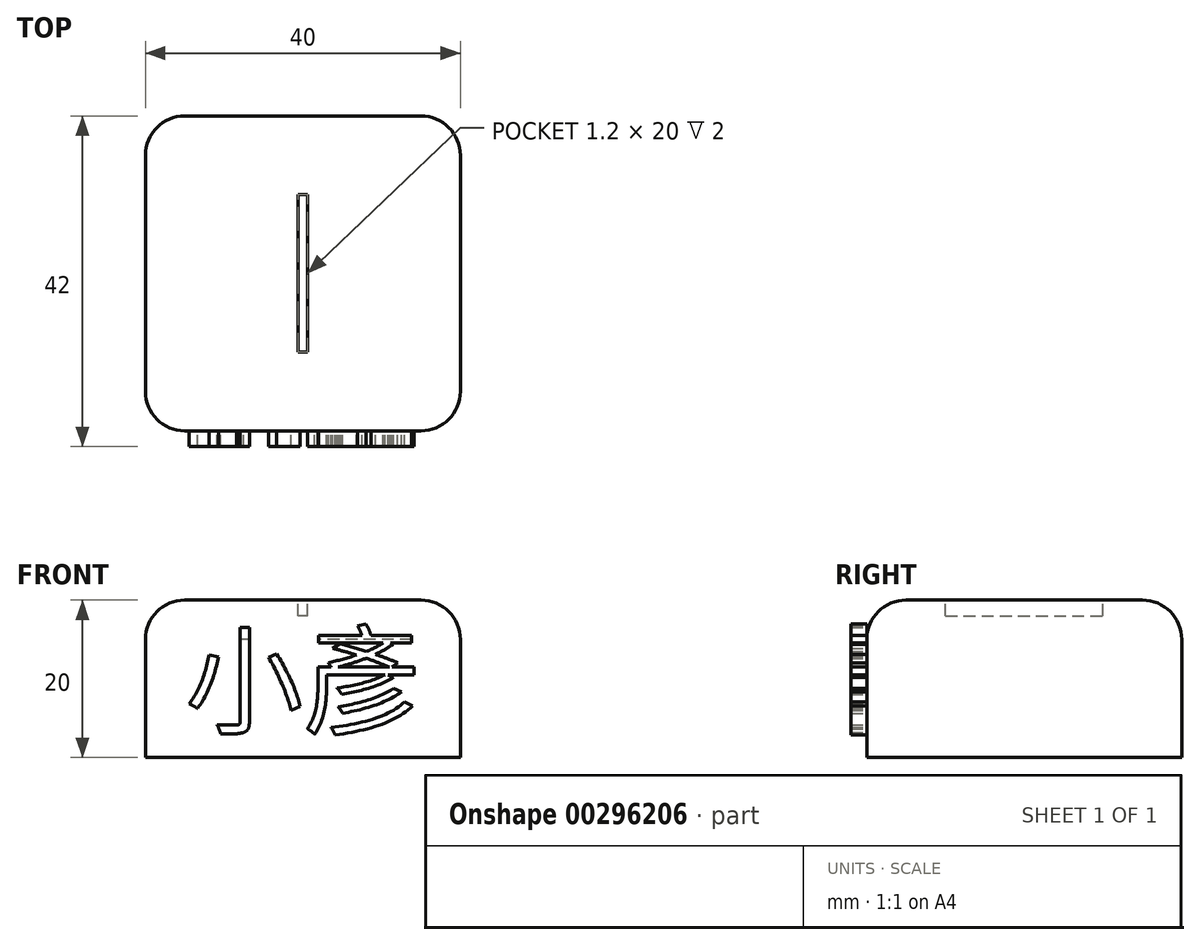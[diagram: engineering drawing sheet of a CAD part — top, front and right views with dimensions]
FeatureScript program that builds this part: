
annotation { "Feature Type Name" : "Feature", "Feature Type Description" : "" }
export const myFeature = defineFeature(function(context is Context, id is Id, definition is map)
    precondition{}
    {
        {
            var Q0;
            Q0=qCreatedBy(makeId("Top.planeOp"),FACE);
            var sketch = newSketch(context, id + "F0", { "sketchPlane" : qUnion([Q0])});
            skLineSegment(sketch, "E0.bottom", {"start": v(20, -20) * mm, "end": v(-20, -20) * mm});
            skLineSegment(sketch, "E0.top", {"start": v(20, 20) * mm, "end": v(-20, 20) * mm});
            skLineSegment(sketch, "E0.left", {"start": v(20, -20) * mm, "end": v(20, 20) * mm});
            skLineSegment(sketch, "E0.right", {"start": v(-20, -20) * mm, "end": v(-20, 20) * mm});
            skPoint(sketch, "E0.middle", {"position": v(0, 0) * mm});
            skLineSegment(sketch, "E1.bottom", {"start": v(0.6, -10) * mm, "end": v(-0.6, -10) * mm});
            skLineSegment(sketch, "E1.top", {"start": v(0.6, 10) * mm, "end": v(-0.6, 10) * mm});
            skLineSegment(sketch, "E1.left", {"start": v(0.6, -10) * mm, "end": v(0.6, 10) * mm});
            skLineSegment(sketch, "E1.right", {"start": v(-0.6, -10) * mm, "end": v(-0.6, 10) * mm});
            skSolve(sketch);
        }
        {
            var Q0;
            Q0=makeQuery(id+"F0.imprint","IMPRINT",FACE,{"disambiguationData":[TD([[makeQuery(id+"F0.imprint","IMPRINT",EDGE,{"derivedFrom":sQuery(id+"F0.wireOp",EDGE,"E0.bottom")}),-1.0]])]});
            var Q1;
            Q1=makeQuery(id+"F0.imprint","IMPRINT",FACE,{"disambiguationData":[TD([[makeQuery(id+"F0.imprint","IMPRINT",EDGE,{"derivedFrom":sQuery(id+"F0.wireOp",EDGE,"E1.bottom")}),-1.0]])]});
            extrude(context, id + "F1", {"entities" : qUnion([Q0, Q1]), "oppositeDirection" : true, "depth" : 20 * mm});
        }
        {
            var Q0;
            Q0=makeQuery(id+"F0.imprint","IMPRINT",FACE,{"disambiguationData":[TD([[makeQuery(id+"F0.imprint","IMPRINT",EDGE,{"derivedFrom":sQuery(id+"F0.wireOp",EDGE,"E1.bottom")}),-1.0]])]});
            extrude(context, id + "F2", {"entities" : qUnion([Q0]), "operationType" : NewBodyOperationType.REMOVE, "oppositeDirection" : true, "depth" : 2 * mm});
        }
        {
            var Q0;
            Q0=makeQuery(id+"F2.boolean.opBoolean","COPY",EDGE,{"derivedFrom":makeQuery(id+"F2.opExtrude","CAP_EDGE",EDGE,{"disambiguationData":[OSD([sQuery(id+"F0.wireOp",EDGE,"E1.left")])],"isStart":true})});
            var Q1;
            Q1=makeQuery(id+"F2.boolean.opBoolean","COPY",EDGE,{"derivedFrom":makeQuery(id+"F2.opExtrude","CAP_EDGE",EDGE,{"disambiguationData":[OSD([sQuery(id+"F0.wireOp",EDGE,"E1.right")])],"isStart":true})});
            var Q2;
            Q2=makeQuery(id+"F1.opExtrude","SWEPT_EDGE",EDGE,{"disambiguationData":[OSD([sQuery(id+"F0.wireOp",EDGE,"E0.bottom"),sQuery(id+"F0.wireOp",EDGE,"E0.left")])]});
            var Q3;
            Q3=makeQuery(id+"F1.opExtrude","SWEPT_EDGE",EDGE,{"disambiguationData":[OSD([sQuery(id+"F0.wireOp",EDGE,"E0.top"),sQuery(id+"F0.wireOp",EDGE,"E0.left")])]});
            var Q4;
            Q4=makeQuery(id+"F1.opExtrude","CAP_EDGE",EDGE,{"disambiguationData":[OSD([sQuery(id+"F0.wireOp",EDGE,"E0.left")])],"isStart":true});
            var Q5;
            Q5=makeQuery(id+"F1.opExtrude","SWEPT_EDGE",EDGE,{"disambiguationData":[OSD([sQuery(id+"F0.wireOp",EDGE,"E0.bottom"),sQuery(id+"F0.wireOp",EDGE,"E0.right")])]});
            var Q6;
            Q6=makeQuery(id+"F1.opExtrude","SWEPT_EDGE",EDGE,{"disambiguationData":[OSD([sQuery(id+"F0.wireOp",EDGE,"E0.top"),sQuery(id+"F0.wireOp",EDGE,"E0.right")])]});
            var Q7;
            Q7=makeQuery(id+"F1.opExtrude","CAP_EDGE",EDGE,{"disambiguationData":[OSD([sQuery(id+"F0.wireOp",EDGE,"E0.top")])],"isStart":true});
            var Q8;
            Q8=makeQuery(id+"F1.opExtrude","CAP_EDGE",EDGE,{"disambiguationData":[OSD([sQuery(id+"F0.wireOp",EDGE,"E0.right")])],"isStart":true});
            var Q9;
            Q9=makeQuery(id+"F1.opExtrude","CAP_EDGE",EDGE,{"disambiguationData":[OSD([sQuery(id+"F0.wireOp",EDGE,"E0.bottom")])],"isStart":true});
            fillet(context, id + "F3", {"entities" : qUnion([Q0, Q1, Q2, Q3, Q4, Q5, Q6, Q7, Q8, Q9]), "radius" : 5 * mm, "tangentPropagation" : true, "allowEdgeOverflow" : false});
        }
        {
            var Q0;
            Q0=makeQuery(id+"F1.opExtrude","SWEPT_FACE",FACE,{"disambiguationData":[OSD([sQuery(id+"F0.wireOp",EDGE,"E0.bottom")])]});
            var sketch = newSketch(context, id + "F4", { "sketchPlane" : qUnion([Q0])});
            skText(sketch, "E2", { "text": "小彥", "fontName": "NotoSansCJKtc-Regular.otf"});
            const initialGuessF4  = {"E2": [-0.015, -0.01587, 1, 0, 0.01087]};
            skSetInitialGuess(sketch, initialGuessF4);
            skSolve(sketch);
        }
        {
            var Q0;
            {var subQ0=sQuery(id+"F4.wireOp",EDGE,"E2.sketch_text.stroke-7");Q0=makeQuery(id+"F4.imprint","IMPRINT",FACE,{"disambiguationData":[TD([[makeQuery(id+"F4.imprint","IMPRINT",EDGE,{"derivedFrom":subQ0}),1.0]])]});}
            var Q1;
            {var subQ6=sQuery(id+"F4.wireOp",EDGE,"E2.sketch_text.stroke-1");Q1=makeQuery(id+"F4.imprint","IMPRINT",FACE,{"disambiguationData":[TD([[makeQuery(id+"F4.imprint","IMPRINT",EDGE,{"derivedFrom":subQ6}),1.0]])]});}
            var Q2;
            Q2=makeQuery(id+"F4.imprint","IMPRINT",FACE,{"disambiguationData":[TD([[makeQuery(id+"F4.imprint","IMPRINT",EDGE,{"derivedFrom":sQuery(id+"F4.wireOp",EDGE,"E2.sketch_text.stroke-12")}),1.0]])]});
            var Q3;
            Q3=makeQuery(id+"F4.imprint","IMPRINT",FACE,{"disambiguationData":[TD([[makeQuery(id+"F4.imprint","IMPRINT",EDGE,{"derivedFrom":sQuery(id+"F4.wireOp",EDGE,"E2.sketch_text.stroke-8")}),1.0]])]});
            var Q4;
            Q4=makeQuery(id+"F4.imprint","IMPRINT",FACE,{"disambiguationData":[TD([[makeQuery(id+"F4.imprint","IMPRINT",EDGE,{"derivedFrom":sQuery(id+"F4.wireOp",EDGE,"E2.sketch_text.stroke-24")}),1.0]])]});
            var Q5;
            Q5=makeQuery(id+"F4.imprint","IMPRINT",FACE,{"disambiguationData":[TD([[makeQuery(id+"F4.imprint","IMPRINT",EDGE,{"derivedFrom":sQuery(id+"F4.wireOp",EDGE,"E2.sketch_text.stroke-20")}),1.0]])]});
            var Q6;
            Q6=makeQuery(id+"F4.imprint","IMPRINT",FACE,{"disambiguationData":[TD([[makeQuery(id+"F4.imprint","IMPRINT",EDGE,{"derivedFrom":sQuery(id+"F4.wireOp",EDGE,"E2.sketch_text.stroke-16")}),1.0]])]});
            extrude(context, id + "F5", {"entities" : qUnion([Q0, Q1, Q2, Q3, Q4, Q5, Q6]), "operationType" : NewBodyOperationType.ADD, "depth" : 2 * mm});
        }
        {
            var Q0;
            {var subQ6=sQuery(id+"F4.wireOp",EDGE,"E2.sketch_text.stroke-33");Q0=makeQuery(id+"F4.imprint","IMPRINT",FACE,{"disambiguationData":[TD([[makeQuery(id+"F4.imprint","IMPRINT",EDGE,{"derivedFrom":subQ6}),1.0]])]});}
            extrude(context, id + "F6", {"entities" : qUnion([Q0]), "operationType" : NewBodyOperationType.ADD, "depth" : 2 * mm});
        }
    });
